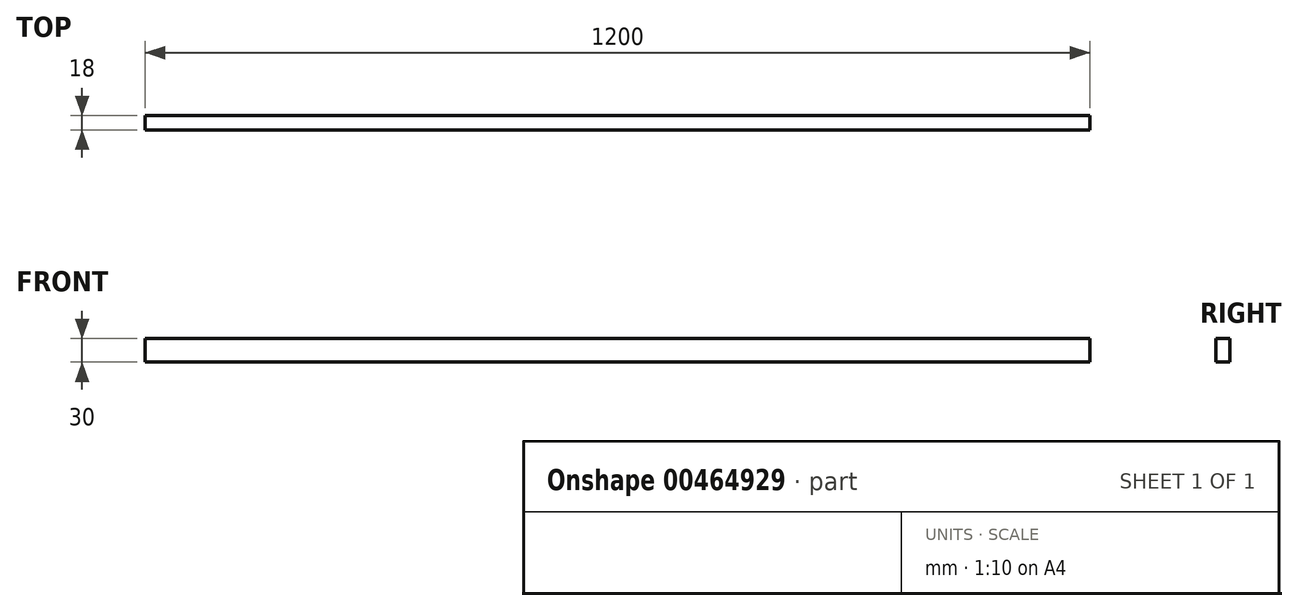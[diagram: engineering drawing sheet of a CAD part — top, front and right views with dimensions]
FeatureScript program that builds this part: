
annotation { "Feature Type Name" : "Feature", "Feature Type Description" : "" }
export const myFeature = defineFeature(function(context is Context, id is Id, definition is map)
    precondition{}
    {
        {
            var Q0;
            Q0=qCreatedBy(makeId("Right.planeOp"),FACE);
            var sketch = newSketch(context, id + "F0", { "sketchPlane" : qUnion([Q0])});
            skLineSegment(sketch, "E0.bottom", {"start": v(-9, 15) * mm, "end": v(9, 15) * mm});
            skLineSegment(sketch, "E0.top", {"start": v(-9, -15) * mm, "end": v(9, -15) * mm});
            skLineSegment(sketch, "E0.left", {"start": v(-9, 15) * mm, "end": v(-9, -15) * mm});
            skLineSegment(sketch, "E0.right", {"start": v(9, 15) * mm, "end": v(9, -15) * mm});
            skPoint(sketch, "E0.middle", {"position": v(0, 0) * mm});
            skSolve(sketch);
        }
        {
            var Q0;
            Q0=makeQuery(id+"F0.imprint","IMPRINT",FACE,{"disambiguationData":[TD([[makeQuery(id+"F0.imprint","IMPRINT",EDGE,{"derivedFrom":sQuery(id+"F0.wireOp",EDGE,"E0.bottom")}),-1.0]])]});
            extrude(context, id + "F1", {"entities" : qUnion([Q0]), "endBound" : BoundingType.SYMMETRIC, "depth" : 1200 * mm, "offsetDistance" : 25 * mm});
        }
    });
